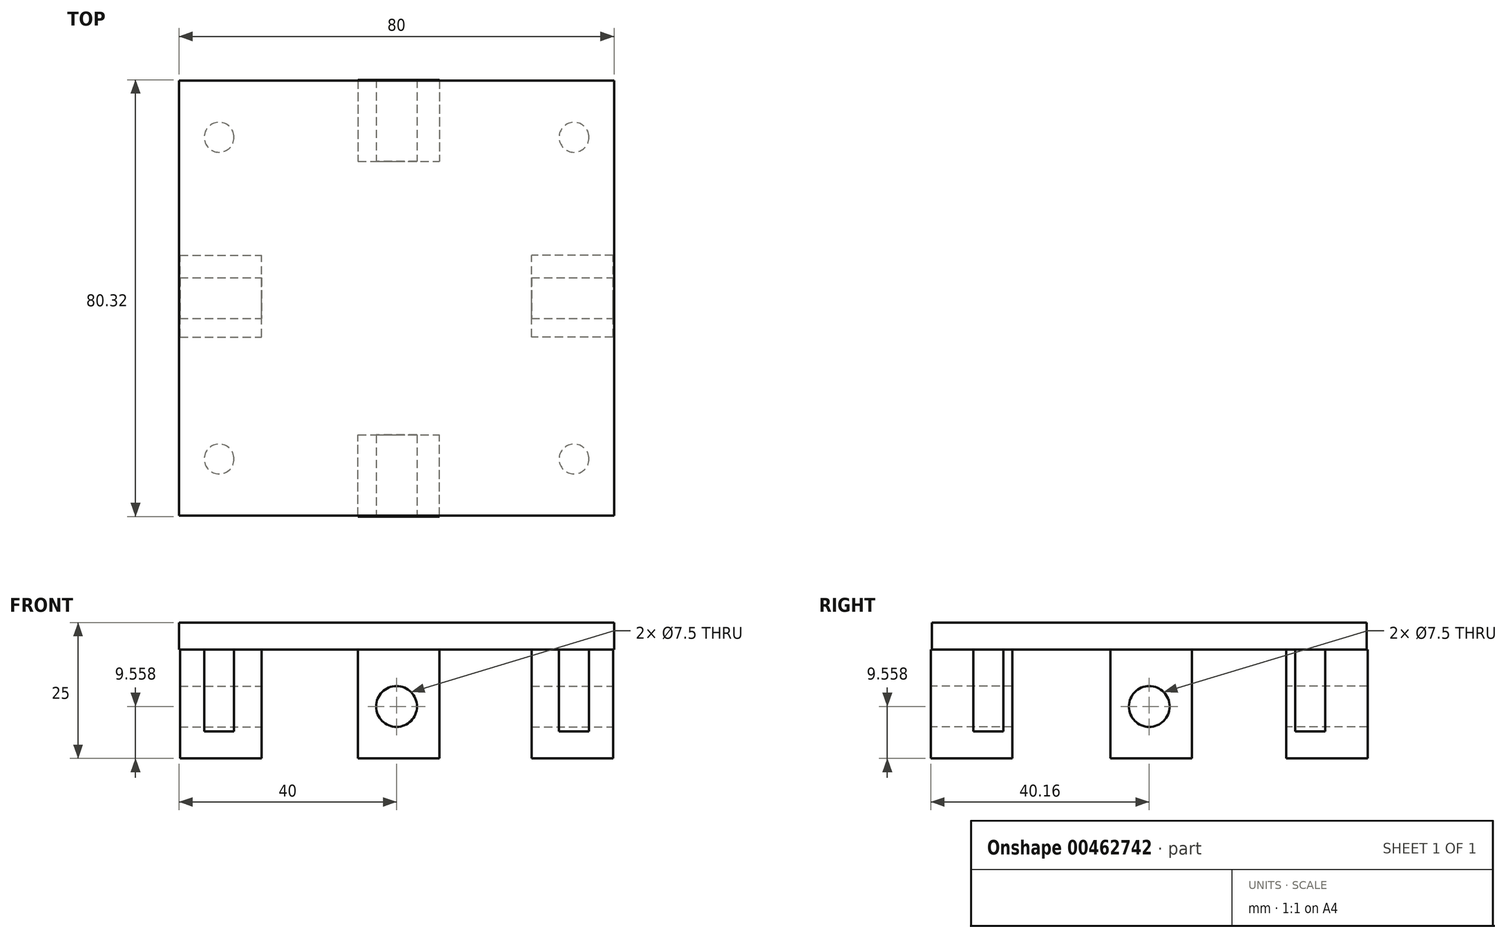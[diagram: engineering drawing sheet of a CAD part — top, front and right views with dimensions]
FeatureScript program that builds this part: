
annotation { "Feature Type Name" : "Feature", "Feature Type Description" : "" }
export const myFeature = defineFeature(function(context is Context, id is Id, definition is map)
    precondition{}
    {
        {
            var Q0;
            Q0=qCreatedBy(makeId("Top.planeOp"),FACE);
            var sketch = newSketch(context, id + "F0", { "sketchPlane" : qUnion([Q0])});
            skLineSegment(sketch, "E0.bottom", {"start": v(40, -40) * mm, "end": v(-40, -40) * mm});
            skLineSegment(sketch, "E0.top", {"start": v(40, 40) * mm, "end": v(-40, 40) * mm});
            skLineSegment(sketch, "E0.left", {"start": v(40, -40) * mm, "end": v(40, 40) * mm});
            skLineSegment(sketch, "E0.right", {"start": v(-40, -40) * mm, "end": v(-40, 40) * mm});
            skPoint(sketch, "E0.middle", {"position": v(0, 0) * mm});
            skSolve(sketch);
        }
        {
            var Q0;
            Q0 = qSketchRegion(id + "F0", true);
            extrude(context, id + "F1", {"entities" : qUnion([Q0]), "depth" : 5 * mm});
        }
        {
            var Q0;
            Q0=qCreatedBy(makeId("Top.planeOp"),FACE);
            var sketch = newSketch(context, id + "F2", { "sketchPlane" : qUnion([Q0])});
            skLineSegment(sketch, "E1.bottom", {"start": v(-37.29, 40.06) * mm, "end": v(-22.29, 40.06) * mm, "construction": true});
            skLineSegment(sketch, "E1.top", {"start": v(-37.29, 25.06) * mm, "end": v(-22.29, 25.06) * mm, "construction": true});
            skLineSegment(sketch, "E1.left", {"start": v(-37.29, 40.06) * mm, "end": v(-37.29, 25.06) * mm, "construction": true});
            skLineSegment(sketch, "E1.right", {"start": v(-22.29, 40.06) * mm, "end": v(-22.29, 25.06) * mm, "construction": true});
            skLineSegment(sketch, "E2.MirrorCS", {"start": v(37.29, 25.06) * mm, "end": v(22.29, 25.06) * mm, "construction": true});
            skLineSegment(sketch, "E3.MirrorCS", {"start": v(22.29, 40.06) * mm, "end": v(22.29, 25.06) * mm, "construction": true});
            skLineSegment(sketch, "E4.MirrorCS", {"start": v(37.29, 40.06) * mm, "end": v(22.29, 40.06) * mm, "construction": true});
            skLineSegment(sketch, "E5.MirrorCS", {"start": v(37.29, 40.06) * mm, "end": v(37.29, 25.06) * mm, "construction": true});
            skLineSegment(sketch, "E6.MirrorCS", {"start": v(-37.29, -25.06) * mm, "end": v(-22.29, -25.06) * mm, "construction": true});
            skLineSegment(sketch, "E7.MirrorCS", {"start": v(-22.29, -40.06) * mm, "end": v(-22.29, -25.06) * mm, "construction": true});
            skLineSegment(sketch, "E8.MirrorCS", {"start": v(-37.29, -40.06) * mm, "end": v(-22.29, -40.06) * mm, "construction": true});
            skLineSegment(sketch, "E9.MirrorCS", {"start": v(-37.29, -40.06) * mm, "end": v(-37.29, -25.06) * mm, "construction": true});
            skLineSegment(sketch, "E10.MirrorCS", {"start": v(37.29, -25.06) * mm, "end": v(22.29, -25.06) * mm, "construction": true});
            skLineSegment(sketch, "E11.MirrorCS", {"start": v(22.29, -40.06) * mm, "end": v(22.29, -25.06) * mm, "construction": true});
            skLineSegment(sketch, "E12.MirrorCS", {"start": v(37.29, -40.06) * mm, "end": v(22.29, -40.06) * mm, "construction": true});
            skLineSegment(sketch, "E13.MirrorCS", {"start": v(37.29, -40.06) * mm, "end": v(37.29, -25.06) * mm, "construction": true});
            skLineSegment(sketch, "E14.MirrorCS", {"start": v(21, 25.03) * mm, "end": v(21, 40.03) * mm});
            skLineSegment(sketch, "E15.MirrorCS", {"start": v(-39.82, 7.86) * mm, "end": v(-24.82, 7.86) * mm});
            skLineSegment(sketch, "E16.MirrorCS", {"start": v(-24.82, -7.14) * mm, "end": v(-24.82, 7.86) * mm});
            skLineSegment(sketch, "E17.MirrorCS", {"start": v(-39.82, -7.14) * mm, "end": v(-24.82, -7.14) * mm});
            skLineSegment(sketch, "E18.MirrorCS", {"start": v(-39.82, -7.14) * mm, "end": v(-39.82, 7.86) * mm});
            skLineSegment(sketch, "E19.MirrorCS", {"start": v(39.82, -7.14) * mm, "end": v(24.82, -7.14) * mm});
            skLineSegment(sketch, "E20.MirrorCS", {"start": v(24.82, -7.14) * mm, "end": v(24.82, 7.86) * mm});
            skLineSegment(sketch, "E21.MirrorCS", {"start": v(39.82, 7.86) * mm, "end": v(24.82, 7.86) * mm});
            skLineSegment(sketch, "E22.MirrorCS", {"start": v(39.82, -7.14) * mm, "end": v(39.82, 7.86) * mm});
            skLineSegment(sketch, "E23.MirrorCS", {"start": v(-7.1, -25.16) * mm, "end": v(7.9, -25.16) * mm});
            skLineSegment(sketch, "E24.MirrorCS", {"start": v(7.9, -40.16) * mm, "end": v(7.9, -25.16) * mm});
            skLineSegment(sketch, "E25.MirrorCS", {"start": v(-7.1, -40.16) * mm, "end": v(7.9, -40.16) * mm});
            skLineSegment(sketch, "E26.MirrorCS", {"start": v(-7.1, -40.16) * mm, "end": v(-7.1, -25.16) * mm});
            skLineSegment(sketch, "E27.MirrorCS", {"start": v(-7.1, 25.16) * mm, "end": v(7.9, 25.16) * mm});
            skLineSegment(sketch, "E28.MirrorCS", {"start": v(-7.1, 40.16) * mm, "end": v(-7.1, 25.16) * mm});
            skLineSegment(sketch, "E29.MirrorCS", {"start": v(-7.1, 40.16) * mm, "end": v(7.9, 40.16) * mm});
            skLineSegment(sketch, "E30.MirrorCS", {"start": v(7.9, 40.16) * mm, "end": v(7.9, 25.16) * mm});
            skSolve(sketch);
        }
        {
            var Q0;
            Q0 = qSketchRegion(id + "F2", true);
            var Q1;
            Q1 = qConstructionFilter(qBodyType(qCreatedBy(id + "F2" ,EDGE), BodyType.WIRE), ConstructionObject.NO);
            extrude(context, id + "F3", {"entities" : qUnion([Q0]), "operationType" : NewBodyOperationType.ADD, "surfaceEntities" : qUnion([Q1]), "oppositeDirection" : true, "depth" : 20 * mm});
        }
        {
            var Q0;
            Q0=qCreatedBy(makeId("Front.planeOp"),FACE);
            cPlane(context, id + "F4", {"entities" : qUnion([Q0]), "cplaneType" : CPlaneType.OFFSET, "offset" : 41.1 * mm, "width" : 150 * mm, "height" : 150 * mm});
        }
        {
            var Q0;
            Q0=qCreatedBy(id+"F4.planeOp",FACE);
            var sketch = newSketch(context, id + "F5", { "sketchPlane" : qUnion([Q0])});
            skPoint(sketch, "E31", {"position": v(0, -10.44) * mm});
            skSolve(sketch);
        }
        {
            var Q0;
            Q0=sQuery(id+"F5.wireOp",VERTEX,"E31");
            var Q1;
            Q1=makeQuery(id+"F1.opExtrude","SWEPT_BODY",BODY,{"disambiguationData":[OSD([sQuery(id+"F0.wireOp",EDGE,"E0.bottom"),sQuery(id+"F0.wireOp",EDGE,"E0.top"),sQuery(id+"F0.wireOp",EDGE,"E0.left"),sQuery(id+"F0.wireOp",EDGE,"E0.right")])]});
            hole(context, id + "F6", {"style" : HoleStyle.SIMPLE, "endStyle" : HoleEndStyle.THROUGH, "holeDiameter" : 7.5 * mm, "isTappedThrough" : true, "tappedDepth" : 12 * mm, "tapClearance" : 3, "locations" : qUnion([Q0]), "scope" : qUnion([Q1])});
        }
        {
            var Q0;
            Q0=qCreatedBy(makeId("Right.planeOp"),FACE);
            cPlane(context, id + "F7", {"entities" : qUnion([Q0]), "cplaneType" : CPlaneType.OFFSET, "offset" : 59.3 * mm, "width" : 150 * mm, "height" : 150 * mm});
        }
        {
            var Q0;
            Q0=qCreatedBy(id+"F7.planeOp",FACE);
            var sketch = newSketch(context, id + "F8", { "sketchPlane" : qUnion([Q0])});
            skPoint(sketch, "E32", {"position": v(0, -10.44) * mm});
            skSolve(sketch);
        }
        {
            var Q0;
            Q0=sQuery(id+"F8.wireOp",VERTEX,"E32");
            var Q1;
            Q1=makeQuery(id+"F1.opExtrude","SWEPT_BODY",BODY,{"disambiguationData":[OSD([sQuery(id+"F0.wireOp",EDGE,"E0.bottom"),sQuery(id+"F0.wireOp",EDGE,"E0.top"),sQuery(id+"F0.wireOp",EDGE,"E0.left"),sQuery(id+"F0.wireOp",EDGE,"E0.right")])]});
            hole(context, id + "F9", {"style" : HoleStyle.SIMPLE, "endStyle" : HoleEndStyle.THROUGH, "holeDiameter" : 7.5 * mm, "isTappedThrough" : true, "tappedDepth" : 12 * mm, "tapClearance" : 3, "locations" : qUnion([Q0]), "scope" : qUnion([Q1])});
        }
        {
            var Q0;
            Q0=qCreatedBy(makeId("Top.planeOp"),FACE);
            var sketch = newSketch(context, id + "F10", { "sketchPlane" : qUnion([Q0])});
            skLineSegment(sketch, "E33.bottom", {"start": v(-40.13, 29.59) * mm, "end": v(-32.63, 29.59) * mm, "construction": true});
            skLineSegment(sketch, "E33.top", {"start": v(-40.13, 37.09) * mm, "end": v(-32.63, 37.09) * mm, "construction": true});
            skLineSegment(sketch, "E33.left", {"start": v(-40.13, 29.59) * mm, "end": v(-40.13, 37.09) * mm, "construction": true});
            skLineSegment(sketch, "E33.right", {"start": v(-32.63, 29.59) * mm, "end": v(-32.63, 37.09) * mm, "construction": true});
            skLineSegment(sketch, "E34", {"start": v(-40.13, 29.59) * mm, "end": v(-32.63, 37.09) * mm, "construction": true});
            skLineSegment(sketch, "E35", {"start": v(-32.63, 29.59) * mm, "end": v(-40.13, 37.09) * mm, "construction": true});
            skCircle(sketch, "E36", {"center": v(-32.63, 29.59) * mm, "radius": 2.75 * mm});
            skCircle(sketch, "E37.MirrorC", {"center": v(32.63, 29.59) * mm, "radius": 2.75 * mm});
            skCircle(sketch, "E38.MirrorC", {"center": v(32.63, -29.59) * mm, "radius": 2.75 * mm});
            skCircle(sketch, "E39.MirrorC", {"center": v(-32.63, -29.59) * mm, "radius": 2.75 * mm});
            skSolve(sketch);
        }
        {
            var Q0;
            Q0 = qSketchRegion(id + "F10", true);
            extrude(context, id + "F11", {"entities" : qUnion([Q0]), "operationType" : NewBodyOperationType.ADD, "oppositeDirection" : true, "depth" : 15 * mm});
        }
    });
